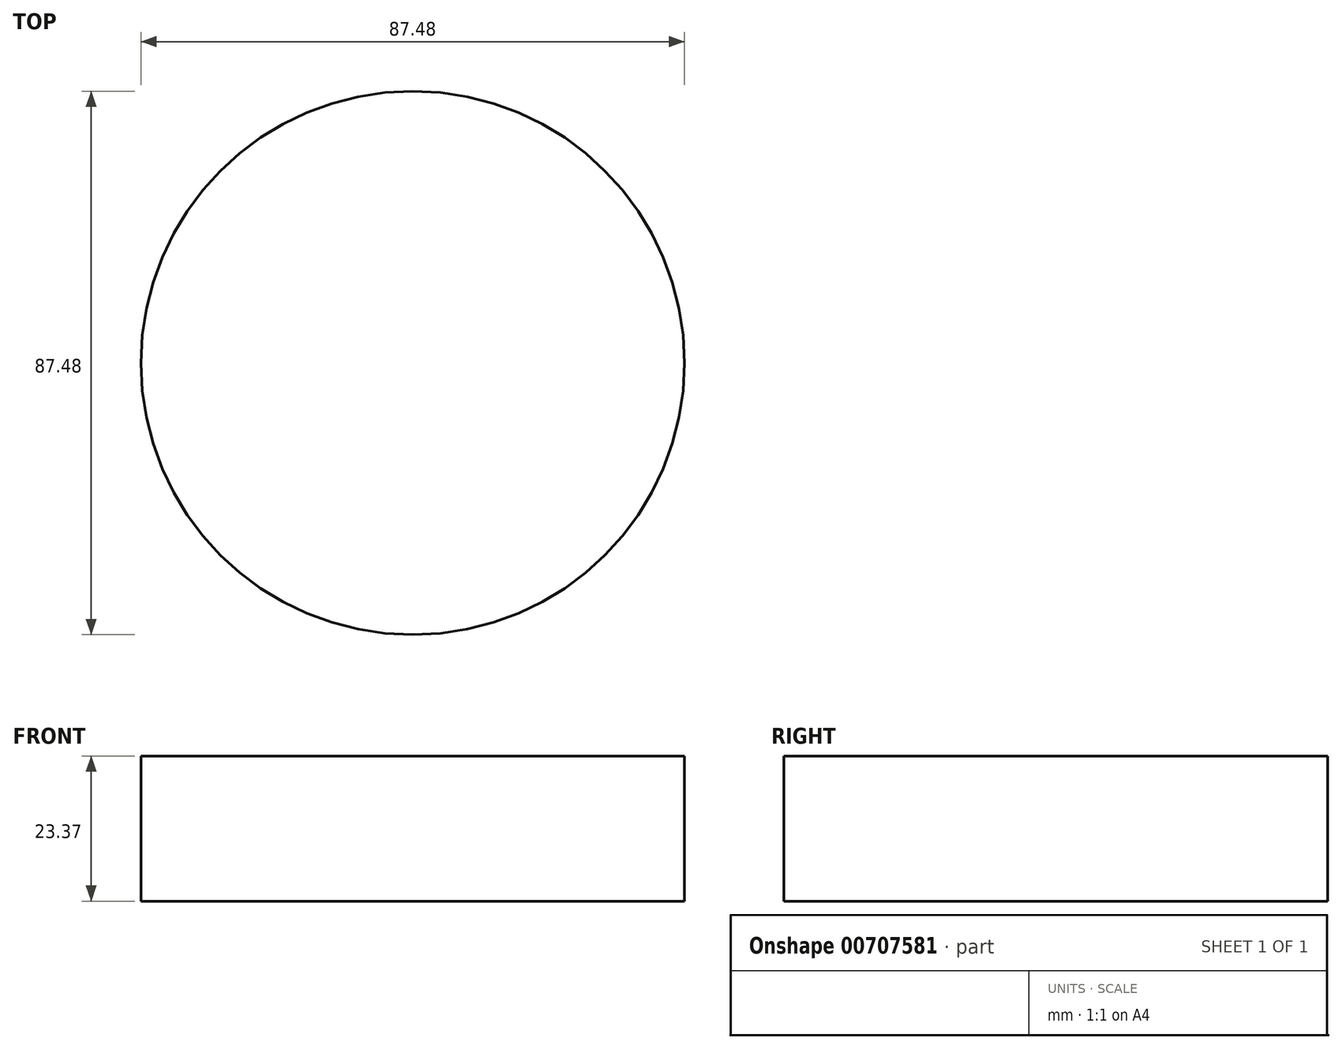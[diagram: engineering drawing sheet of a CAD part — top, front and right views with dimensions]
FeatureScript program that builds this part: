
annotation { "Feature Type Name" : "Feature", "Feature Type Description" : "" }
export const myFeature = defineFeature(function(context is Context, id is Id, definition is map)
    precondition{}
    {
        {
            var Q0;
            Q0=qCreatedBy(makeId("Top.planeOp"),FACE);
            var sketch = newSketch(context, id + "F0", { "sketchPlane" : qUnion([Q0])});
            skCircle(sketch, "E0", {"center": v(0, 0) * mm, "radius": 43.74 * mm});
            skSolve(sketch);
        }
        {
            var Q0;
            Q0 = qSketchRegion(id + "F0", true);
            extrude(context, id + "F1", {"entities" : qUnion([Q0]), "depth" : 23.37 * mm, "offsetDistance" : 25.4 * mm});
        }
    });
